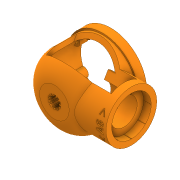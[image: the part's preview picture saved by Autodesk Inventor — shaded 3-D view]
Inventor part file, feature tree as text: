
AUTODESK INVENTOR PART (.ipt)
format: ipt  version: 2020 (Build 240168000, 168)  size: 998,912 bytes
history: native  units: in
note: dims shown in document units (in); Inventor stores cm internally (conversion verified against a paired STEP export)
features: chamfer x35, sketch x25, extrude x22, plane x8, projected_geometry x5, revolve x1, fillet x1, emboss x1
ambient origin geometry x8: Origin, YZ Plane, XZ Plane, XY Plane, X Axis, Y Axis, Z Axis, Center Point
bodies: Solid1 (feature_tree)
feature tree (98):
  extrude  "Extrusion1"  Depth=0.315in TaperAngle=0.0deg
  chamfer  "Chamfer1"  Distance=0.315in
  extrude  "Extrusion2"  Depth=2.3622in TaperAngle=360.0deg
  extrude  "Extrusion3"  Depth=0.0197in TaperAngle=0.0deg
  extrude  "Extrusion4"  Depth=0.1575in TaperAngle=0.0deg
  extrude  "Extrusion5"  Depth=1.2598in TaperAngle=0.0deg
  revolve  "Revolution1"  [1 undecoded]
  plane  "Work Plane1"
  extrude  "Extrusion6"  Depth=0.1575in
  plane  "Work Plane2"
  plane  "Work Plane3"
  extrude  "Extrusion8"  [1 undecoded]
  extrude  "Extrusion9"  Depth=0.1575in TaperAngle=0.0deg
  chamfer  "Chamfer3"  Distance=1.8898in
  extrude  "Extrusion10"  Depth=1.2795in
  plane  "Work Plane4"
  extrude  "Extrusion11"  Depth=0.315in TaperAngle=0.0deg
  extrude  "Extrusion12"  Depth=0.2756in
  extrude  "Extrusion13"  Depth=3.1496in TaperAngle=360.0deg
  chamfer  "Chamfer4"  Distance=0.2756in
  chamfer  "Chamfer5"  Distance=0.9843in
  chamfer  "Chamfer6"  Distance=0.315in
  chamfer  "Chamfer7"  Distance=3.937in Angle=360.0deg
  chamfer  "Chamfer8"  Distance=0.315in
  chamfer  "Chamfer9"  Distance=0.315in
  chamfer  "Chamfer10"  Distance=0.315in
  chamfer  "Chamfer11"  Distance=0.315in
  chamfer  "Chamfer12"  Distance=0.315in
  chamfer  "Chamfer13"  Distance=0.315in
  chamfer  "Chamfer14"  Distance=0.315in
  chamfer  "Chamfer15"  Distance=0.315in
  chamfer  "Chamfer16"  Distance=0.315in
  chamfer  "Chamfer17"  Distance=0.315in
  chamfer  "Chamfer18"  Distance=0.315in
  chamfer  "Chamfer19"  Distance=0.315in
  chamfer  "Chamfer20"  Distance=0.315in
  chamfer  "Chamfer21"  Distance=0.315in
  chamfer  "Chamfer22"  Distance=0.315in
  chamfer  "Chamfer23"  Distance=0.315in
  chamfer  "Chamfer24"  Distance=0.315in
  chamfer  "Chamfer25"  Distance=0.315in
  chamfer  "Chamfer26"  Distance=0.315in
  chamfer  "Chamfer27"  Distance=0.315in
  chamfer  "Chamfer28"  Distance=0.315in
  chamfer  "Chamfer29"  Distance=0.315in
  chamfer  "Chamfer30"  Distance=0.315in
  chamfer  "Chamfer31"  Distance=0.315in
  chamfer  "Chamfer32"  Distance=0.315in
  chamfer  "Chamfer33"  Distance=0.315in
  plane  "Work Plane5"
  extrude  "Extrusion15"  Depth=0.315in
  extrude  "Extrusion16"  Depth=0.315in
  plane  "Work Plane6"
  extrude  "Extrusion18"  Depth=0.9843in
  extrude  "Extrusion20"  TaperAngle=60.0deg  [1 undecoded]
  extrude  "Extrusion21"  TaperAngle=0.0deg  [1 undecoded]
  extrude  "Extrusion22"  Depth=2.3622in TaperAngle=0.0deg
  chamfer  "Chamfer34"  Distance=0.2067in
  chamfer  "Chamfer35"  Distance=0.0787in
  fillet  "Fillet1"  [1 undecoded]
  plane  "Work Plane7"
  emboss  "Emboss1"
  chamfer  "Chamfer36"  Distance=0.1969in
  sketch  "Sketch25"  dims[d162=0.315in d163=0.125in d164=0.0137in d166=0.9843in]
  plane  "Work Plane8"
  extrude  "Extrusion23"  [1 undecoded]
  extrude  "Extrusion24"  Depth=0.4921in TaperAngle=0.0deg
  extrude  "Extrusion25"  Depth=0.4921in
  extrude  "Extrusion26"  Depth=0.4921in TaperAngle=0.0deg
  sketch  "Sketch1"  dims[d0=0.4724in d1=0.315in d2=0.0in d3=0.315in d4=0.125in d5=0.0137in]
  sketch  "Sketch2"  dims[d6=0.0157in d7=2.3622in d9=360.0deg]
  sketch  "Sketch3"  dims[d11=0.315in d12=0.0in d13=0.0197in d14=0.0in]
  projected_geometry  "Projected Loop1"
  sketch  "Sketch4"  dims[d15=2.5591in d16=0.1575in d17=0.0in]
  sketch  "Sketch5"  dims[d18=0.1575in d19=1.2598in d20=0.0in]
  sketch  "Sketch6"  dims[d21=1.1024in d22=0.5512in]
  sketch  "Sketch7"  dims[d23=0.8465in d24=0.1575in]
  sketch  "Sketch9"  dims[d25=90.0deg d26=-2.1063in]
  sketch  "Sketch10"  dims[d27=0.1575in d28=0.1575in d29=0.0in d33=-0.1575in d41=1.8898in]
  sketch  "Sketch11"  dims[d42=1.2795in d43=1.8898in]
  sketch  "Sketch12"  dims[d44=0.2165in d45=0.315in d46=0.0in]
  sketch  "Sketch13"  dims[d47=1.1811in d48=0.0in d49=0.2756in d50=0.125in d51=0.0137in]
  sketch  "Sketch14"  dims[d52=0.0157in d53=3.1496in d55=360.0deg d57=0.2756in d58=0.0in]
  sketch  "Sketch16"  dims[d59=-0.2756in d61=0.9843in d62=0.0in]
  sketch  "Sketch17"  dims[d63=0.4764in d64=0.315in d65=0.0in]
  sketch  "Sketch19"  dims[d66=0.0787in]
  projected_geometry  "Projected Loop2"
  projected_geometry  "Projected Loop3"
  sketch  "Sketch21"  dims[d67=0.0787in]
  sketch  "Sketch22"  dims[d68=0.0394in d69=3.937in d71=360.0deg d73=0.315in d74=0.0in d75=0.315in d76=0.125in d77=0.0137in d78=0.315in d79=0.125in d80=0.0137in d81=0.315in d82=0.125in d83=0.0137in d84=0.315in d85=0.125in d86=0.0137in d87=0.315in d88=0.125in d89=0.0137in d90=0.315in d91=0.125in d92=0.0137in d93=0.315in d94=0.125in d95=0.0137in d96=0.315in d97=0.125in d98=0.0137in d99=0.315in d100=0.125in d101=0.0137in d102=0.315in d103=0.125in d104=0.0137in d105=0.315in d106=0.125in d107=0.0137in d108=0.315in d109=0.125in d110=0.0137in d111=0.315in d112=0.125in d113=0.0137in d114=0.315in d115=0.125in d116=0.0137in d117=0.315in d118=0.125in d119=0.0137in d120=0.315in d121=0.125in d122=0.0137in d123=0.315in d124=0.125in d125=0.0137in d126=0.315in d127=0.125in d128=0.0137in d129=0.315in d130=0.125in d131=0.0137in d132=0.315in d133=0.125in d134=0.0137in d135=0.315in d136=0.125in d137=0.0137in d138=0.315in d139=0.125in d140=0.0137in d141=0.315in d142=0.125in d143=0.0137in d144=0.315in d145=0.125in d146=0.0137in d147=0.315in d148=0.125in d149=0.0137in]
  sketch  "Sketch23"  dims[d150=0.315in d151=0.125in d152=0.0137in d153=0.315in d154=0.125in d155=0.0137in]
  projected_geometry  "Projected Loop4"
  sketch  "Sketch24"  dims[d156=0.315in d157=0.125in d158=0.0137in d159=0.315in d160=0.125in d161=0.0137in]
  sketch  "Sketch28"  dims[d171=-0.2756in d172=60.0deg]
  sketch  "Sketch29"  dims[d173=60.0deg d174=0.0in]
  sketch  "Sketch30"  dims[d175=0.0in d176=2.3622in d177=0.0in]
  projected_geometry  "Projected Loop5"
  sketch  "Sketch31"  dims[d178=0.315in d179=0.2067in d180=0.0787in d181=45.0deg d182=0.1969in d183=0.0in d187=-0.4921in d188=0.1969in d189=0.0in d193=0.315in d194=0.0984in d195=0.0in d196=0.2362in d197=0.0984in d198=0.0in d199=0.0984in d200=0.0in d201=0.0591in d202=0.125in d203=0.0137in d204=0.0591in d205=0.125in d206=0.0137in d207=0.0197in d209=0.0394in d210=0.0in d211=0.0787in d212=0.125in d213=0.0137in d214=2.126in d215=-0.1575in d217=0.4921in d218=0.0in d220=4.7244in d221=0.1083in d222=0.1575in d223=360.0deg d224=0.1969in d225=0.1969in d226=0.1969in d227=0.1969in d228=0.1969in d229=0.1969in d230=0.1969in d231=0.1969in d232=0.1969in d233=0.1969in d234=0.0787in d235=0.0787in d236=0.0787in d237=0.0787in d238=0.0787in d239=0.0787in d240=0.0787in d241=0.0787in d242=0.0787in d243=0.0787in d244=0.315in d245=0.0in d246=0.315in d247=0.0in d248=0.0591in d249=0.315in d250=0.0in]
note: 6 required parameter values undecoded (feature->parameter linkage not recoverable at this tier; creation-order binding heuristic only, values carry confidence <= 0.55)